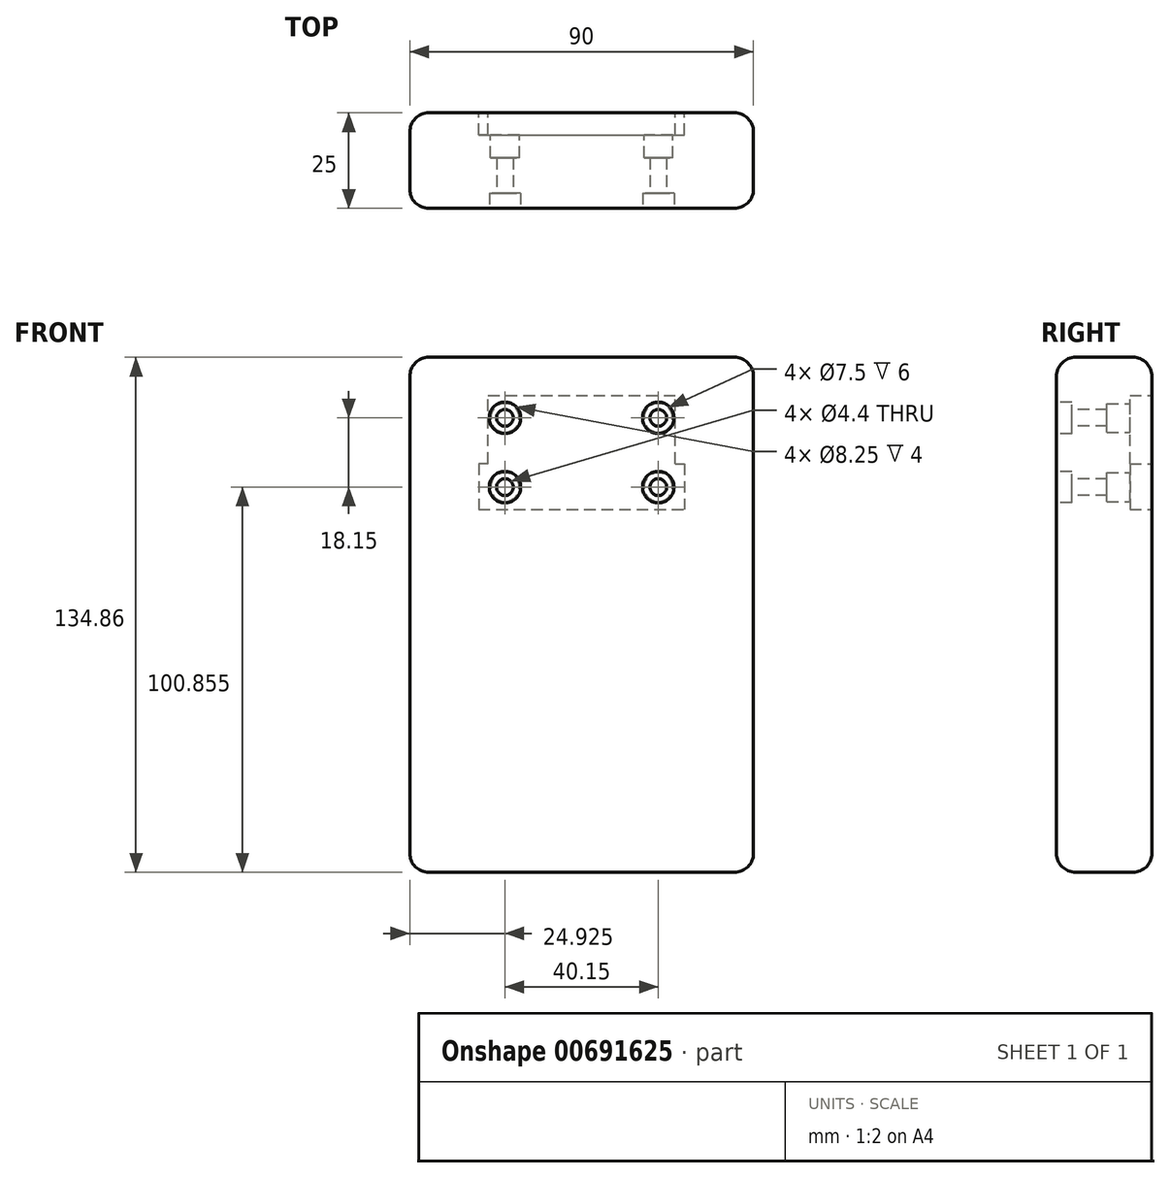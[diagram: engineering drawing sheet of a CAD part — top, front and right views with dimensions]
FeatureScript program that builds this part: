
annotation { "Feature Type Name" : "Feature", "Feature Type Description" : "" }
export const myFeature = defineFeature(function(context is Context, id is Id, definition is map)
    precondition{}
    {
        {
            var Q0;
            Q0=qCreatedBy(makeId("Front.planeOp"),FACE);
            var sketch = newSketch(context, id + "F0", { "sketchPlane" : qUnion([Q0])});
            skLineSegment(sketch, "E0.bottom", {"start": v(-40, 10) * mm, "end": v(40, 10) * mm});
            skLineSegment(sketch, "E0.top", {"start": v(-40, -124.86) * mm, "end": v(40, -124.86) * mm});
            skLineSegment(sketch, "E0.left", {"start": v(-45, 5) * mm, "end": v(-45, -119.86) * mm});
            skLineSegment(sketch, "E0.right", {"start": v(45, 5) * mm, "end": v(45, -119.86) * mm});
            skPoint(sketch, "E1.visualSharp", {"position": v(-45, 10) * mm});
            skArc(sketch, "E1.filletArc", {"start": v(-40, 10) * mm, "mid": v(-43.54, 8.54) * mm, "end": v(-45, 5) * mm});
            skPoint(sketch, "E2.visualSharp", {"position": v(45, 10) * mm});
            skArc(sketch, "E2.filletArc", {"start": v(45, 5) * mm, "mid": v(43.54, 8.54) * mm, "end": v(40, 10) * mm});
            skPoint(sketch, "E3.visualSharp", {"position": v(45, -124.86) * mm});
            skArc(sketch, "E3.filletArc", {"start": v(40, -124.86) * mm, "mid": v(43.54, -123.4) * mm, "end": v(45, -119.86) * mm});
            skPoint(sketch, "E4.visualSharp", {"position": v(-45, -124.86) * mm});
            skArc(sketch, "E4.filletArc", {"start": v(-45, -119.86) * mm, "mid": v(-43.54, -123.4) * mm, "end": v(-40, -124.86) * mm});
            skSolve(sketch);
        }
        {
            var Q0;
            Q0=makeQuery(id+"F0.imprint","IMPRINT",FACE,{"disambiguationData":[TD([[makeQuery(id+"F0.imprint","IMPRINT",EDGE,{"derivedFrom":sQuery(id+"F0.wireOp",EDGE,"E0.bottom")}),-1.0]])]});
            extrude(context, id + "F1", {"entities" : qUnion([Q0]), "depth" : 25 * mm, "offsetDistance" : 25 * mm});
        }
        {
            var Q0;
            Q0=qCreatedBy(makeId("Front.planeOp"),FACE);
            var sketch = newSketch(context, id + "F2", { "sketchPlane" : qUnion([Q0])});
            skLineSegment(sketch, "E5.bottom", {"start": v(-24.46, 0) * mm, "end": v(24.46, 0) * mm});
            skLineSegment(sketch, "E5.top", {"start": v(-26.95, -29.86) * mm, "end": v(26.96, -29.86) * mm});
            skLineSegment(sketch, "E5.left", {"start": v(-26.95, -17.86) * mm, "end": v(-26.95, -29.86) * mm});
            skLineSegment(sketch, "E5.right", {"start": v(26.96, -17.86) * mm, "end": v(26.96, -29.86) * mm});
            skLineSegment(sketch, "E6", {"start": v(-20.08, -5.86) * mm, "end": v(20.08, -5.86) * mm});
            skLineSegment(sketch, "E7", {"start": v(20.08, -5.86) * mm, "end": v(20.08, -24) * mm});
            skLineSegment(sketch, "E8", {"start": v(-20.08, -24) * mm, "end": v(20.08, -24) * mm});
            skLineSegment(sketch, "E9", {"start": v(-20.08, -24) * mm, "end": v(-20.08, -5.86) * mm});
            skCircle(sketch, "E10", {"center": v(-20.08, -5.86) * mm, "radius": 1.63 * mm});
            skCircle(sketch, "E11", {"center": v(20.08, -5.86) * mm, "radius": 1.63 * mm});
            skCircle(sketch, "E12", {"center": v(20.08, -24) * mm, "radius": 1.63 * mm});
            skCircle(sketch, "E13", {"center": v(-20.08, -24) * mm, "radius": 1.63 * mm});
            skCircle(sketch, "E14", {"center": v(-20.08, -5.86) * mm, "radius": 3.75 * mm});
            skCircle(sketch, "E15", {"center": v(20.08, -5.86) * mm, "radius": 3.75 * mm});
            skCircle(sketch, "E16", {"center": v(20.08, -24) * mm, "radius": 3.75 * mm});
            skCircle(sketch, "E17", {"center": v(-20.08, -24) * mm, "radius": 3.75 * mm});
            skLineSegment(sketch, "E18.left", {"start": v(-24.46, -17.86) * mm, "end": v(-24.46, 0) * mm});
            skLineSegment(sketch, "E18.right", {"start": v(24.46, -17.86) * mm, "end": v(24.46, 0) * mm});
            skLineSegment(sketch, "E19", {"start": v(-24.46, -17.86) * mm, "end": v(-26.95, -17.86) * mm});
            skLineSegment(sketch, "E20", {"start": v(24.46, -17.86) * mm, "end": v(26.96, -17.86) * mm});
            skSolve(sketch);
        }
        {
            var Q0;
            Q0=makeQuery(id+"F2.imprint","IMPRINT",FACE,{"disambiguationData":[TD([[makeQuery(id+"F2.imprint","IMPRINT",EDGE,{"derivedFrom":sQuery(id+"F2.wireOp",EDGE,"E5.top")}),1.0]])]});
            var Q1;
            {var subQ3=sQuery(id+"F2.wireOp",EDGE,"E14");var subQ13=sQuery(id+"F2.wireOp",EDGE,"E6");var subQ14=makeQuery(id+"F2.imprint","INTERSECT",VERTEX,{"derivedFrom":[subQ13,subQ3]});Q1=makeQuery(id+"F2.imprint","IMPRINT",FACE,{"disambiguationData":[TD([[makeQuery(id+"F2.imprint","IMPRINT",EDGE,{"disambiguationData":[TD([[subQ14,-1.0]])],"derivedFrom":subQ13}),-1.0]])]});}
            extrude(context, id + "F3", {"entities" : qUnion([Q0, Q1]), "operationType" : NewBodyOperationType.REMOVE, "depth" : 5.78 * mm, "offsetDistance" : 25 * mm});
        }
        {
            var Q0;
            {var subQ0=sQuery(id+"F2.wireOp",EDGE,"E10");var subQ1=sQuery(id+"F2.wireOp",EDGE,"E6");var subQ2=makeQuery(id+"F2.imprint","INTERSECT",VERTEX,{"derivedFrom":[subQ1,subQ0]});Q0=makeQuery(id+"F2.imprint","IMPRINT",FACE,{"disambiguationData":[TD([[makeQuery(id+"F2.imprint","IMPRINT",EDGE,{"disambiguationData":[TD([[subQ2,-1.0]])],"derivedFrom":subQ1}),-1.0]])]});}
            var Q1;
            {var subQ0=sQuery(id+"F2.wireOp",EDGE,"E9");var subQ1=sQuery(id+"F2.wireOp",EDGE,"E6");var subQ2=makeQuery(id+"F2.imprint","INTERSECT",VERTEX,{"derivedFrom":[subQ1,subQ0]});Q1=makeQuery(id+"F2.imprint","IMPRINT",FACE,{"disambiguationData":[TD([[makeQuery(id+"F2.imprint","IMPRINT",EDGE,{"disambiguationData":[TD([[subQ2,-1.0]])],"derivedFrom":subQ1}),-1.0]])]});}
            var Q2;
            {var subQ0=sQuery(id+"F2.wireOp",EDGE,"E9");var subQ1=sQuery(id+"F2.wireOp",EDGE,"E6");var subQ2=makeQuery(id+"F2.imprint","INTERSECT",VERTEX,{"derivedFrom":[subQ1,subQ0]});Q2=makeQuery(id+"F2.imprint","IMPRINT",FACE,{"disambiguationData":[TD([[makeQuery(id+"F2.imprint","IMPRINT",EDGE,{"disambiguationData":[TD([[subQ2,-1.0]])],"derivedFrom":subQ1}),1.0]])]});}
            var Q3;
            {var subQ0=sQuery(id+"F2.wireOp",EDGE,"E10");var subQ1=sQuery(id+"F2.wireOp",EDGE,"E6");var subQ2=makeQuery(id+"F2.imprint","INTERSECT",VERTEX,{"derivedFrom":[subQ1,subQ0]});Q3=makeQuery(id+"F2.imprint","IMPRINT",FACE,{"disambiguationData":[TD([[makeQuery(id+"F2.imprint","IMPRINT",EDGE,{"disambiguationData":[TD([[subQ2,-1.0]])],"derivedFrom":subQ1}),1.0]])]});}
            var Q4;
            {var subQ0=sQuery(id+"F2.wireOp",EDGE,"E13");var subQ1=sQuery(id+"F2.wireOp",EDGE,"E8");var subQ2=makeQuery(id+"F2.imprint","INTERSECT",VERTEX,{"derivedFrom":[subQ1,subQ0]});Q4=makeQuery(id+"F2.imprint","IMPRINT",FACE,{"disambiguationData":[TD([[makeQuery(id+"F2.imprint","IMPRINT",EDGE,{"disambiguationData":[TD([[subQ2,-1.0]])],"derivedFrom":subQ1}),1.0]])]});}
            var Q5;
            {var subQ0=sQuery(id+"F2.wireOp",EDGE,"E9");var subQ1=sQuery(id+"F2.wireOp",EDGE,"E8");var subQ2=makeQuery(id+"F2.imprint","INTERSECT",VERTEX,{"derivedFrom":[subQ1,subQ0]});Q5=makeQuery(id+"F2.imprint","IMPRINT",FACE,{"disambiguationData":[TD([[makeQuery(id+"F2.imprint","IMPRINT",EDGE,{"disambiguationData":[TD([[subQ2,-1.0]])],"derivedFrom":subQ1}),1.0]])]});}
            var Q6;
            {var subQ0=sQuery(id+"F2.wireOp",EDGE,"E13");var subQ1=sQuery(id+"F2.wireOp",EDGE,"E8");var subQ2=makeQuery(id+"F2.imprint","INTERSECT",VERTEX,{"derivedFrom":[subQ1,subQ0]});Q6=makeQuery(id+"F2.imprint","IMPRINT",FACE,{"disambiguationData":[TD([[makeQuery(id+"F2.imprint","IMPRINT",EDGE,{"disambiguationData":[TD([[subQ2,-1.0]])],"derivedFrom":subQ1}),-1.0]])]});}
            var Q7;
            {var subQ0=sQuery(id+"F2.wireOp",EDGE,"E9");var subQ1=sQuery(id+"F2.wireOp",EDGE,"E8");var subQ2=makeQuery(id+"F2.imprint","INTERSECT",VERTEX,{"derivedFrom":[subQ1,subQ0]});Q7=makeQuery(id+"F2.imprint","IMPRINT",FACE,{"disambiguationData":[TD([[makeQuery(id+"F2.imprint","IMPRINT",EDGE,{"disambiguationData":[TD([[subQ2,-1.0]])],"derivedFrom":subQ1}),-1.0]])]});}
            var Q8;
            {var subQ0=sQuery(id+"F2.wireOp",EDGE,"E15");var subQ1=sQuery(id+"F2.wireOp",EDGE,"E6");var subQ2=makeQuery(id+"F2.imprint","INTERSECT",VERTEX,{"derivedFrom":[subQ1,subQ0]});Q8=makeQuery(id+"F2.imprint","IMPRINT",FACE,{"disambiguationData":[TD([[makeQuery(id+"F2.imprint","IMPRINT",EDGE,{"disambiguationData":[TD([[subQ2,-1.0]])],"derivedFrom":subQ1}),-1.0]])]});}
            var Q9;
            {var subQ0=sQuery(id+"F2.wireOp",EDGE,"E7");var subQ1=sQuery(id+"F2.wireOp",EDGE,"E6");var subQ2=makeQuery(id+"F2.imprint","INTERSECT",VERTEX,{"derivedFrom":[subQ1,subQ0]});Q9=makeQuery(id+"F2.imprint","IMPRINT",FACE,{"disambiguationData":[TD([[makeQuery(id+"F2.imprint","IMPRINT",EDGE,{"disambiguationData":[TD([[subQ2,1.0]])],"derivedFrom":subQ1}),-1.0]])]});}
            var Q10;
            {var subQ0=sQuery(id+"F2.wireOp",EDGE,"E15");var subQ1=sQuery(id+"F2.wireOp",EDGE,"E6");var subQ2=makeQuery(id+"F2.imprint","INTERSECT",VERTEX,{"derivedFrom":[subQ1,subQ0]});Q10=makeQuery(id+"F2.imprint","IMPRINT",FACE,{"disambiguationData":[TD([[makeQuery(id+"F2.imprint","IMPRINT",EDGE,{"disambiguationData":[TD([[subQ2,-1.0]])],"derivedFrom":subQ1}),1.0]])]});}
            var Q11;
            {var subQ0=sQuery(id+"F2.wireOp",EDGE,"E7");var subQ1=sQuery(id+"F2.wireOp",EDGE,"E6");var subQ2=makeQuery(id+"F2.imprint","INTERSECT",VERTEX,{"derivedFrom":[subQ1,subQ0]});Q11=makeQuery(id+"F2.imprint","IMPRINT",FACE,{"disambiguationData":[TD([[makeQuery(id+"F2.imprint","IMPRINT",EDGE,{"disambiguationData":[TD([[subQ2,1.0]])],"derivedFrom":subQ1}),1.0]])]});}
            var Q12;
            {var subQ0=sQuery(id+"F2.wireOp",EDGE,"E16");var subQ1=sQuery(id+"F2.wireOp",EDGE,"E7");var subQ2=makeQuery(id+"F2.imprint","INTERSECT",VERTEX,{"derivedFrom":[subQ1,subQ0]});Q12=makeQuery(id+"F2.imprint","IMPRINT",FACE,{"disambiguationData":[TD([[makeQuery(id+"F2.imprint","IMPRINT",EDGE,{"disambiguationData":[TD([[subQ2,-1.0]])],"derivedFrom":subQ1}),-1.0]])]});}
            var Q13;
            {var subQ0=sQuery(id+"F2.wireOp",EDGE,"E8");var subQ1=sQuery(id+"F2.wireOp",EDGE,"E7");var subQ2=makeQuery(id+"F2.imprint","INTERSECT",VERTEX,{"derivedFrom":[subQ1,subQ0]});Q13=makeQuery(id+"F2.imprint","IMPRINT",FACE,{"disambiguationData":[TD([[makeQuery(id+"F2.imprint","IMPRINT",EDGE,{"disambiguationData":[TD([[subQ2,1.0]])],"derivedFrom":subQ1}),-1.0]])]});}
            var Q14;
            {var subQ0=sQuery(id+"F2.wireOp",EDGE,"E8");var subQ1=sQuery(id+"F2.wireOp",EDGE,"E7");var subQ2=makeQuery(id+"F2.imprint","INTERSECT",VERTEX,{"derivedFrom":[subQ1,subQ0]});Q14=makeQuery(id+"F2.imprint","IMPRINT",FACE,{"disambiguationData":[TD([[makeQuery(id+"F2.imprint","IMPRINT",EDGE,{"disambiguationData":[TD([[subQ2,1.0]])],"derivedFrom":subQ1}),1.0]])]});}
            var Q15;
            {var subQ0=sQuery(id+"F2.wireOp",EDGE,"E16");var subQ1=sQuery(id+"F2.wireOp",EDGE,"E7");var subQ2=makeQuery(id+"F2.imprint","INTERSECT",VERTEX,{"derivedFrom":[subQ1,subQ0]});Q15=makeQuery(id+"F2.imprint","IMPRINT",FACE,{"disambiguationData":[TD([[makeQuery(id+"F2.imprint","IMPRINT",EDGE,{"disambiguationData":[TD([[subQ2,-1.0]])],"derivedFrom":subQ1}),1.0]])]});}
            var Q16;
            Q16=makeQuery(id+"F3.boolean.opBoolean","COPY",FACE,{"derivedFrom":makeQuery(id+"F3.opExtrude","CAP_FACE",FACE,{"disambiguationData":[OSD([sQuery(id+"F2.wireOp",EDGE,"E5.top"),sQuery(id+"F2.wireOp",EDGE,"E5.left"),sQuery(id+"F2.wireOp",EDGE,"E5.right"),sQuery(id+"F2.wireOp",EDGE,"E14"),sQuery(id+"F2.wireOp",EDGE,"E15"),sQuery(id+"F2.wireOp",EDGE,"E16"),sQuery(id+"F2.wireOp",EDGE,"E17"),sQuery(id+"F2.wireOp",EDGE,"E5.bottom"),sQuery(id+"F2.wireOp",EDGE,"E18.left"),sQuery(id+"F2.wireOp",EDGE,"E18.right"),sQuery(id+"F2.wireOp",EDGE,"E19"),sQuery(id+"F2.wireOp",EDGE,"E20")])],"isStart":false})});
            extrude(context, id + "F4", {"entities" : qUnion([Q0, Q1, Q2, Q3, Q4, Q5, Q6, Q7, Q8, Q9, Q10, Q11, Q12, Q13, Q14, Q15]), "operationType" : NewBodyOperationType.REMOVE, "endBound" : BoundingType.UP_TO_SURFACE, "depth" : 8 * mm, "endBoundEntityFace" : qUnion([Q16]), "hasOffset" : true, "offsetDistance" : 6 * mm, "offsetOppositeDirection" : true});
        }
        {
            var Q0;
            Q0=makeQuery(id+"F1.opExtrude","CAP_EDGE",EDGE,{"disambiguationData":[OSD([sQuery(id+"F0.wireOp",EDGE,"E0.top")])],"isStart":true});
            var Q1;
            Q1=makeQuery(id+"F1.opExtrude","CAP_EDGE",EDGE,{"disambiguationData":[OSD([sQuery(id+"F0.wireOp",EDGE,"E4.filletArc")])],"isStart":true});
            var Q2;
            Q2=makeQuery(id+"F1.opExtrude","CAP_EDGE",EDGE,{"disambiguationData":[OSD([sQuery(id+"F0.wireOp",EDGE,"E3.filletArc")])],"isStart":true});
            var Q3;
            Q3=makeQuery(id+"F1.opExtrude","CAP_EDGE",EDGE,{"disambiguationData":[OSD([sQuery(id+"F0.wireOp",EDGE,"E0.right")])],"isStart":true});
            var Q4;
            Q4=makeQuery(id+"F1.opExtrude","CAP_EDGE",EDGE,{"disambiguationData":[OSD([sQuery(id+"F0.wireOp",EDGE,"E0.left")])],"isStart":true});
            var Q5;
            Q5=makeQuery(id+"F1.opExtrude","CAP_EDGE",EDGE,{"disambiguationData":[OSD([sQuery(id+"F0.wireOp",EDGE,"E0.bottom")])],"isStart":true});
            var Q6;
            Q6=makeQuery(id+"F1.opExtrude","CAP_EDGE",EDGE,{"disambiguationData":[OSD([sQuery(id+"F0.wireOp",EDGE,"E1.filletArc")])],"isStart":true});
            var Q7;
            Q7=makeQuery(id+"F1.opExtrude","CAP_EDGE",EDGE,{"disambiguationData":[OSD([sQuery(id+"F0.wireOp",EDGE,"E2.filletArc")])],"isStart":true});
            fillet(context, id + "F5", {"entities" : qUnion([Q0, Q1, Q2, Q3, Q4, Q5, Q6, Q7]), "radius" : 5 * mm, "allowEdgeOverflow" : false});
        }
        {
            var Q0;
            Q0=makeQuery(id+"F1.opExtrude","CAP_EDGE",EDGE,{"disambiguationData":[OSD([sQuery(id+"F0.wireOp",EDGE,"E0.top")])],"isStart":false});
            fillet(context, id + "F6", {"entities" : qUnion([Q0]), "radius" : 5 * mm, "tangentPropagation" : true, "allowEdgeOverflow" : false});
        }
        {
            var Q0;
            Q0=makeQuery(id+"F1.opExtrude","CAP_FACE",FACE,{"disambiguationData":[OSD([sQuery(id+"F0.wireOp",EDGE,"E0.bottom"),sQuery(id+"F0.wireOp",EDGE,"E0.top"),sQuery(id+"F0.wireOp",EDGE,"E0.left"),sQuery(id+"F0.wireOp",EDGE,"E0.right"),sQuery(id+"F0.wireOp",EDGE,"E1.filletArc"),sQuery(id+"F0.wireOp",EDGE,"E2.filletArc"),sQuery(id+"F0.wireOp",EDGE,"E3.filletArc"),sQuery(id+"F0.wireOp",EDGE,"E4.filletArc")])],"isStart":false});
            var sketch = newSketch(context, id + "F7", { "sketchPlane" : qUnion([Q0])});
            skPoint(sketch, "E21.0", {"position": v(-20.08, -5.86) * mm});
            skPoint(sketch, "E22.0", {"position": v(20.08, -5.86) * mm});
            skPoint(sketch, "E23.0", {"position": v(20.08, -24) * mm});
            skPoint(sketch, "E24.0", {"position": v(-20.08, -24) * mm});
            skSolve(sketch);
        }
        {
            var Q0;
            Q0=sQuery(id+"F7.wireOp",VERTEX,"E24.0");
            var Q1;
            Q1=sQuery(id+"F7.wireOp",VERTEX,"E21.0");
            var Q2;
            Q2=sQuery(id+"F7.wireOp",VERTEX,"E22.0");
            var Q3;
            Q3=sQuery(id+"F7.wireOp",VERTEX,"E23.0");
            var Q4;
            Q4=makeQuery(id+"F1.opExtrude","SWEPT_BODY",BODY,{"disambiguationData":[OSD([sQuery(id+"F0.wireOp",EDGE,"E0.bottom"),sQuery(id+"F0.wireOp",EDGE,"E0.top"),sQuery(id+"F0.wireOp",EDGE,"E0.left"),sQuery(id+"F0.wireOp",EDGE,"E0.right"),sQuery(id+"F0.wireOp",EDGE,"E1.filletArc"),sQuery(id+"F0.wireOp",EDGE,"E2.filletArc"),sQuery(id+"F0.wireOp",EDGE,"E3.filletArc"),sQuery(id+"F0.wireOp",EDGE,"E4.filletArc")])]});
            hole(context, id + "F8", {"style" : HoleStyle.C_BORE, "endStyle" : HoleEndStyle.THROUGH, "standardTappedOrClearance" : lookupTablePath({ "standard" : "ISO", "fit" : "Normal", "size" : "M4", "type" : "Clearance" }), "standardBlindInLast" : lookupTablePath({ "fit" : "Standard", "standard" : "ISO", "size" : "M4", "type" : "Clearance" }), "holeDiameter" : 4.4 * mm, "cBoreDiameter" : 8.25 * mm, "cBoreDepth" : 4 * mm, "majorDiameter" : 4 * mm, "isTappedThrough" : true, "tappedDepth" : 5.6 * mm, "tapClearance" : 3, "locations" : qUnion([Q0, Q1, Q2, Q3]), "scope" : qUnion([Q4])});
        }
    });
